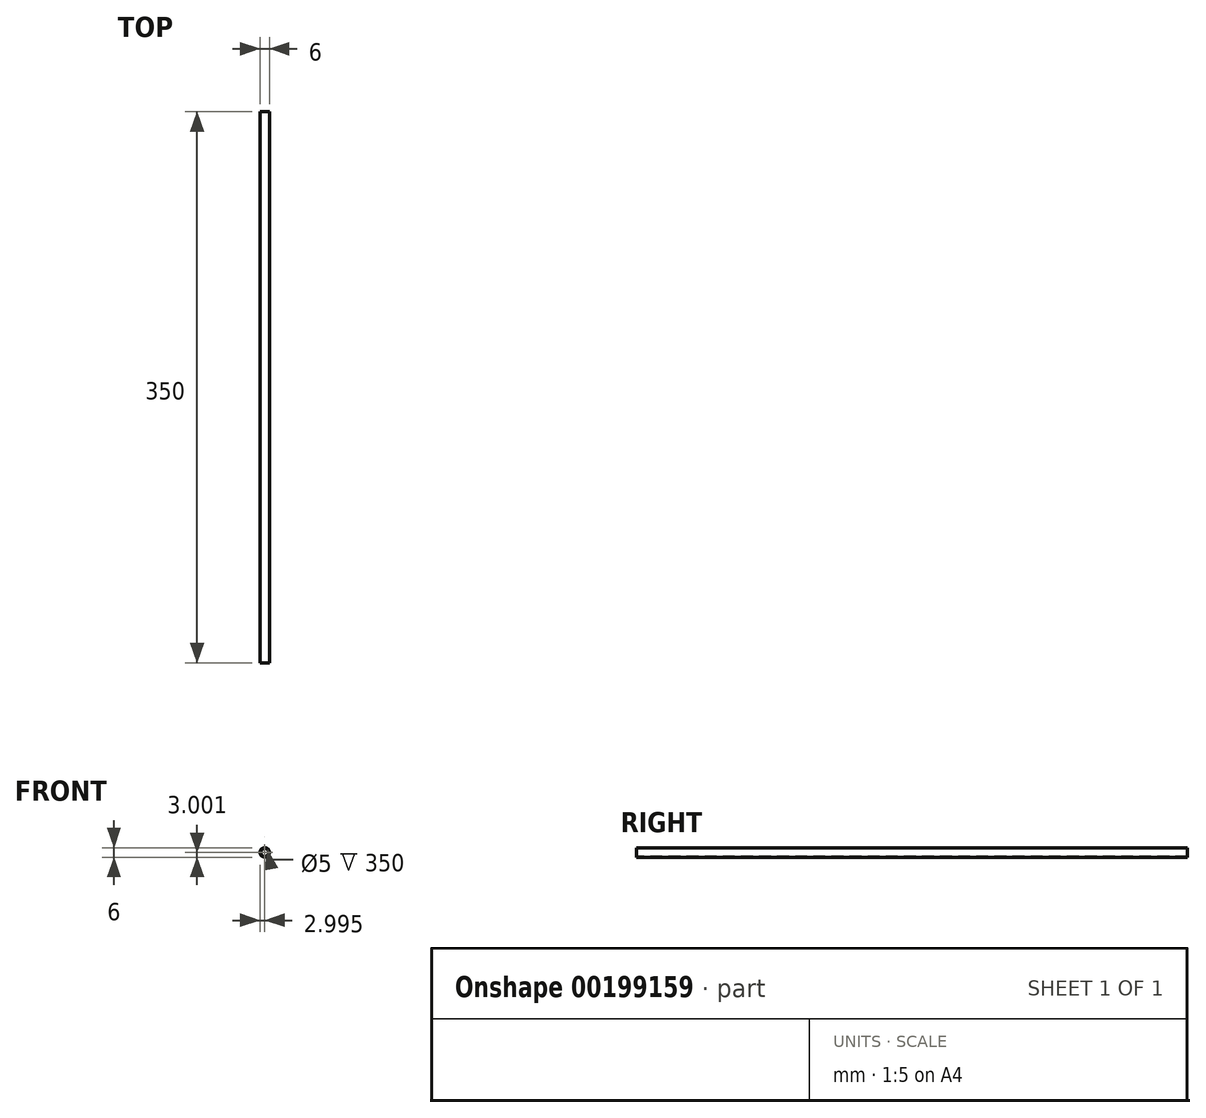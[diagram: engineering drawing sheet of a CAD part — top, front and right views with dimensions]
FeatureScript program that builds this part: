
annotation { "Feature Type Name" : "Feature", "Feature Type Description" : "" }
export const myFeature = defineFeature(function(context is Context, id is Id, definition is map)
    precondition{}
    {
        {
            var Q0;
            Q0=qCreatedBy(makeId("Front.planeOp"),FACE);
            var sketch = newSketch(context, id + "F0", { "sketchPlane" : qUnion([Q0])});
            skCircle(sketch, "E0", {"center": v(-5.34, 5.18) * mm, "radius": 3 * mm});
            skCircle(sketch, "E1", {"center": v(-5.34, 5.18) * mm, "radius": 2.5 * mm});
            skSolve(sketch);
        }
        {
            var Q0;
            Q0 = qSketchRegion(id + "F0", true);
            extrude(context, id + "F1", {"entities" : qUnion([Q0]), "oppositeDirection" : true, "depth" : 350 * mm});
        }
    });
